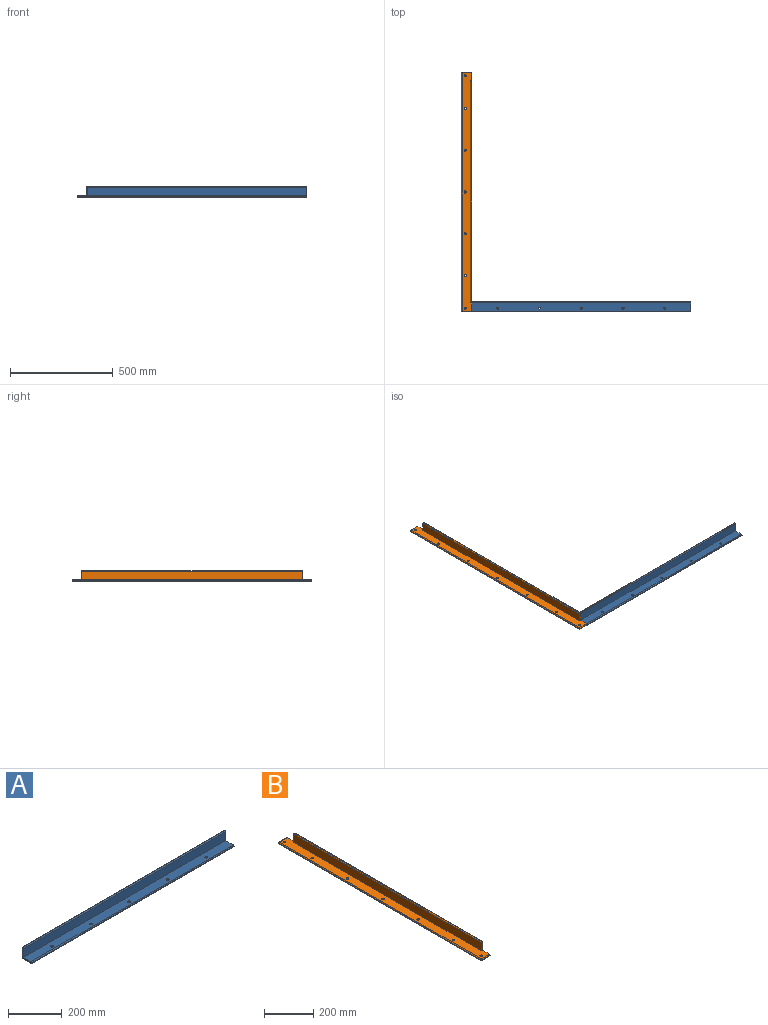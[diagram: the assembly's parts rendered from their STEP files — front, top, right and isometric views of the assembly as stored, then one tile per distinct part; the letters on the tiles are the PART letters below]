
ASSEMBLY  parts=2 mates=1
PART A: 15 faces, bbox 1066.8x50.8x50.8 mm
  f0: cylinder r=5.16mm len=10.31mm, axis (0,0,1), area 226.3mm2, adj f5,f8
  f1: cylinder r=5.16mm len=10.31mm, axis (0,0,1), area 226.3mm2, adj f5,f8
  f2: cylinder r=5.16mm len=10.31mm, axis (0,0,1), area 226.3mm2, adj f5,f8
  f3: cylinder r=5.16mm len=10.31mm, axis (0,0,1), area 226.3mm2, adj f5,f8
  f4: plane 50.8x50.8mm, normal (-1,0,0), area 654.7mm2, adj f5,f6,f7,f8,f9,f10,f11,f12
  f5: plane 1066.8x50.8mm, normal (0,0,-1), area 53775.8mm2, adj f0,f1,f2,f3,f4,f6,f12,f13
  f6: plane 1066.8x3.18mm, normal (0,-1,0), area 3387.1mm2, adj f4,f5,f7,f13
  f7: cylinder r=3.81mm len=1066.8mm, axis (-1,0,0), area 6384.5mm2, adj f4,f6,f8,f13
  f8: plane 1066.8x40.01mm, normal (0,0,1), area 42259.7mm2, adj f0,f1,f2,f3,f4,f7,f9,f13
  f9: plane 1066.8x40.01mm, normal (0,-1,0), area 42677.3mm2, adj f4,f8,f10,f13
  f10: cylinder r=3.81mm len=1066.8mm, axis (-1,0,0), area 6384.5mm2, adj f4,f9,f11,f13
  f11: plane 1066.8x3.18mm, normal (0,0,1), area 3387.1mm2, adj f4,f10,f12,f13
  f12: plane 1066.8x50.8mm, normal (0,1,0), area 54193.4mm2, adj f4,f5,f11,f13
  f13: plane 50.8x50.8mm, normal (1,0,0), area 654.7mm2, adj f5,f6,f7,f8,f9,f10,f11,f12
  f14: cylinder r=5.16mm len=10.31mm, axis (0,0,1), area 226.3mm2, adj f5,f8
PART B: 23 faces, bbox 50.8x1168.4x50.8 mm
  f0: cylinder r=5.16mm len=10.31mm, axis (0,0,1), area 226.3mm2, adj f8,f11
  f1: cylinder r=5.16mm len=10.31mm, axis (0,0,1), area 226.3mm2, adj f8,f11
  f2: cylinder r=5.16mm len=10.31mm, axis (0,0,1), area 226.3mm2, adj f8,f11
  f3: cylinder r=5.16mm len=10.31mm, axis (0,0,1), area 226.3mm2, adj f8,f11
  f4: cylinder r=3.81mm len=1080.77mm, axis (0,1,0), area 6451.5mm2, adj f5,f13,f14,f19
  f5: plane 1080.77x40.01mm, normal (-1,0,0), area 43236.2mm2, adj f4,f11,f12,f18
  f6: cylinder r=3.81mm len=1168.4mm, axis (0,1,0), area 6976mm2, adj f7,f10,f11,f17
  f7: plane 1168.4x3.18mm, normal (-1,0,0), area 3709.7mm2, adj f6,f8,f9,f16
  f8: plane 1168.4x50.8mm, normal (0,0,-1), area 58770.1mm2, adj f0,f1,f2,f3,f7,f9,f15,f16
  f9: plane 50.8x3.18mm, normal (0,-1,0), area 161.3mm2, adj f7,f8,f10,f15
  f10: cylinder r=3.81mm len=50.8mm, axis (-1,0,0), area 295.7mm2, adj f6,f9,f11,f15
  f11: plane 1160.78x46.99mm, normal (0,0,1), area 46411.2mm2, adj f0,f1,f2,f3,f5,f6,f10,f12
  f12: plane 40.01x6.99mm, normal (0,-1,0), area 279.4mm2, adj f5,f11,f13,f15
  f13: cylinder r=3.81mm len=6.99mm, axis (-1,0,0), area 33.5mm2, adj f4,f12,f14,f15
  f14: plane 1073.15x3.18mm, normal (0,0,1), area 3407.3mm2, adj f4,f13,f15,f19
  f15: plane 1168.4x50.8mm, normal (1,0,0), area 55502.8mm2, adj f8,f9,f10,f11,f12,f13,f14,f16
  f16: plane 50.8x3.18mm, normal (0,1,0), area 161.3mm2, adj f7,f8,f15,f17
  f17: cylinder r=3.81mm len=50.8mm, axis (1,0,0), area 295.7mm2, adj f6,f11,f15,f16
  f18: plane 40.01x6.99mm, normal (0,1,0), area 279.4mm2, adj f5,f11,f15,f19
  f19: cylinder r=3.81mm len=6.99mm, axis (1,0,0), area 33.5mm2, adj f4,f14,f15,f18
  f20: cylinder r=5.16mm len=10.31mm, axis (0,0,1), area 226.3mm2, adj f8,f11
  f21: cylinder r=5.16mm len=10.31mm, axis (0,0,1), area 226.3mm2, adj f8,f11
  f22: cylinder r=5.16mm len=10.31mm, axis (0,0,1), area 226.3mm2, adj f8,f11
PLACE A at identity
PLACE B at identity
MATE fastened A.f5 <-> B.f8  axis (0,0,-1) through (-533.4,-584.2,-2133.6)mm
